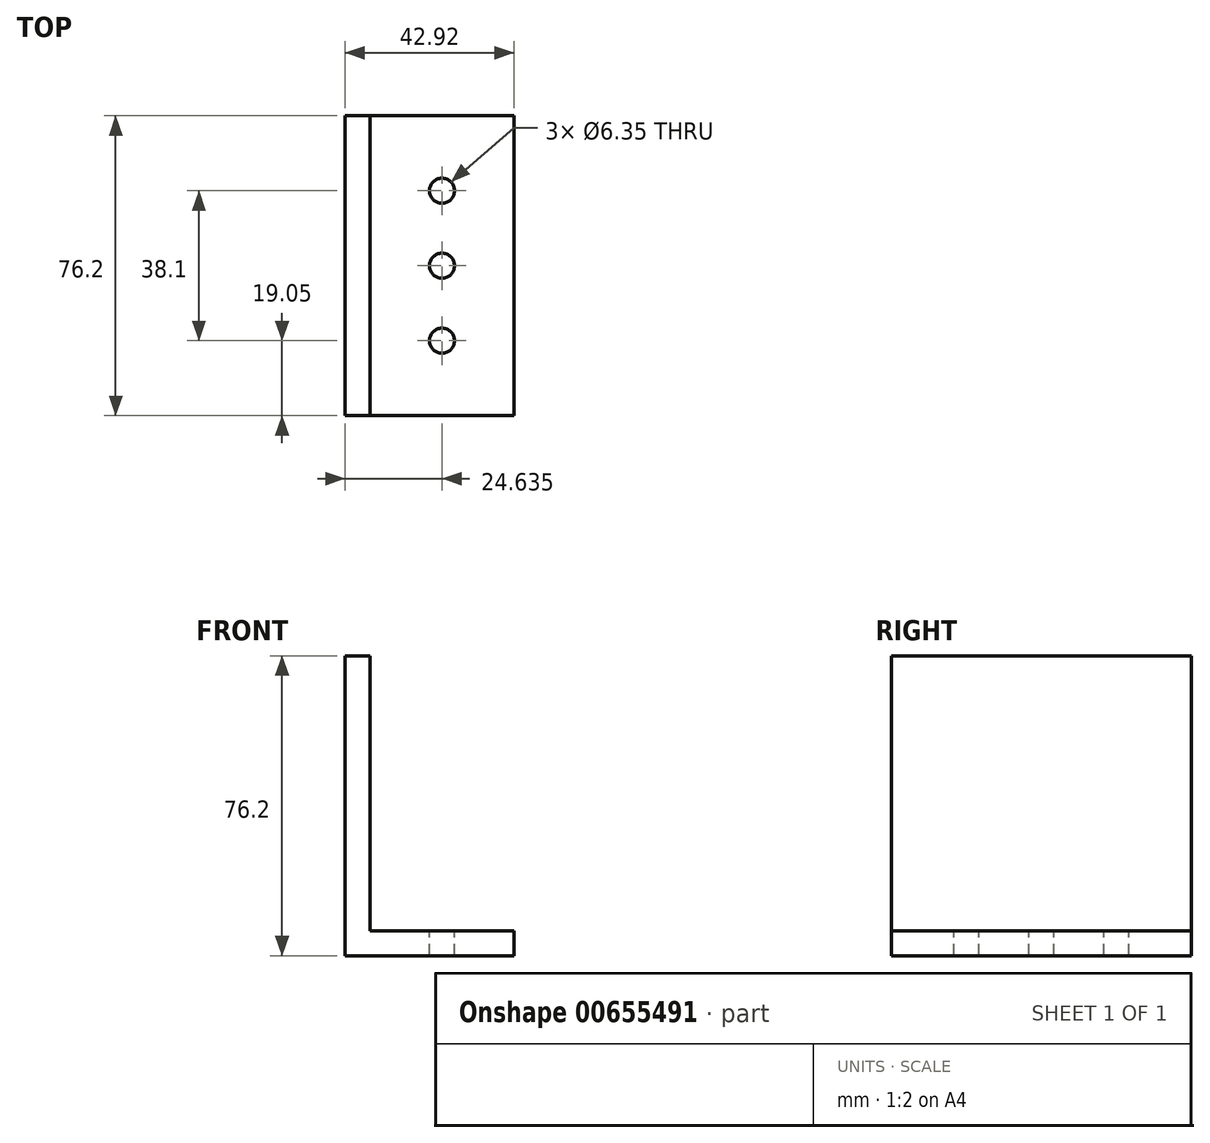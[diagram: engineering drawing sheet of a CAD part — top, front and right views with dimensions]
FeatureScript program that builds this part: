
annotation { "Feature Type Name" : "Feature", "Feature Type Description" : "" }
export const myFeature = defineFeature(function(context is Context, id is Id, definition is map)
    precondition{}
    {
        {
            var Q0;
            Q0=qCreatedBy(makeId("Front.planeOp"),FACE);
            var sketch = newSketch(context, id + "F0", { "sketchPlane" : qUnion([Q0])});
            skLineSegment(sketch, "E0", {"start": v(0, 0) * mm, "end": v(0, 76.2) * mm});
            skLineSegment(sketch, "E1", {"start": v(0, 76.2) * mm, "end": v(6.35, 76.2) * mm});
            skLineSegment(sketch, "E2", {"start": v(6.35, 76.2) * mm, "end": v(6.35, 6.35) * mm});
            skLineSegment(sketch, "E3", {"start": v(6.35, 6.35) * mm, "end": v(42.92, 6.35) * mm});
            skLineSegment(sketch, "E4", {"start": v(42.92, 6.35) * mm, "end": v(42.92, 0) * mm});
            skLineSegment(sketch, "E5", {"start": v(42.92, 0) * mm, "end": v(0, 0) * mm});
            skSolve(sketch);
        }
        {
            var Q0;
            Q0=makeQuery(id+"F0.imprint","IMPRINT",FACE,{"disambiguationData":[TD([[makeQuery(id+"F0.imprint","IMPRINT",EDGE,{"derivedFrom":sQuery(id+"F0.wireOp",EDGE,"E0")}),-1.0]])]});
            extrude(context, id + "F1", {"entities" : qUnion([Q0]), "depth" : 76.2 * mm, "offsetDistance" : 25.4 * mm});
        }
        {
            var Q0;
            Q0=makeQuery(id+"F1.opExtrude","SWEPT_FACE",FACE,{"disambiguationData":[OSD([sQuery(id+"F0.wireOp",EDGE,"E3")])]});
            var sketch = newSketch(context, id + "F2", { "sketchPlane" : qUnion([Q0])});
            skCircle(sketch, "E6", {"center": v(24.63, -19.05) * mm, "radius": 3.18 * mm});
            skCircle(sketch, "E7", {"center": v(24.63, -38.1) * mm, "radius": 3.18 * mm});
            skCircle(sketch, "E8", {"center": v(24.63, -57.15) * mm, "radius": 3.18 * mm});
            skLineSegment(sketch, "E9", {"start": v(24.63, 0) * mm, "end": v(24.63, -19.05) * mm, "construction": true});
            skLineSegment(sketch, "E10", {"start": v(24.63, -19.05) * mm, "end": v(24.63, -38.1) * mm, "construction": true});
            skLineSegment(sketch, "E11", {"start": v(24.63, -38.1) * mm, "end": v(24.63, -57.15) * mm, "construction": true});
            skLineSegment(sketch, "E12", {"start": v(24.63, -57.15) * mm, "end": v(24.63, -76.2) * mm, "construction": true});
            skSolve(sketch);
        }
        {
            var Q0;
            Q0=makeQuery(id+"F2.imprint","IMPRINT",FACE,{"disambiguationData":[TD([[makeQuery(id+"F2.imprint","IMPRINT",EDGE,{"derivedFrom":sQuery(id+"F2.wireOp",EDGE,"E6")}),1.0]])]});
            var Q1;
            Q1=makeQuery(id+"F2.imprint","IMPRINT",FACE,{"disambiguationData":[TD([[makeQuery(id+"F2.imprint","IMPRINT",EDGE,{"derivedFrom":sQuery(id+"F2.wireOp",EDGE,"E7")}),1.0]])]});
            var Q2;
            Q2=makeQuery(id+"F2.imprint","IMPRINT",FACE,{"disambiguationData":[TD([[makeQuery(id+"F2.imprint","IMPRINT",EDGE,{"derivedFrom":sQuery(id+"F2.wireOp",EDGE,"E8")}),1.0]])]});
            extrude(context, id + "F3", {"entities" : qUnion([Q0, Q1, Q2]), "operationType" : NewBodyOperationType.REMOVE, "endBound" : BoundingType.THROUGH_ALL, "oppositeDirection" : true, "depth" : 25.4 * mm, "offsetDistance" : 25.4 * mm});
        }
    });
